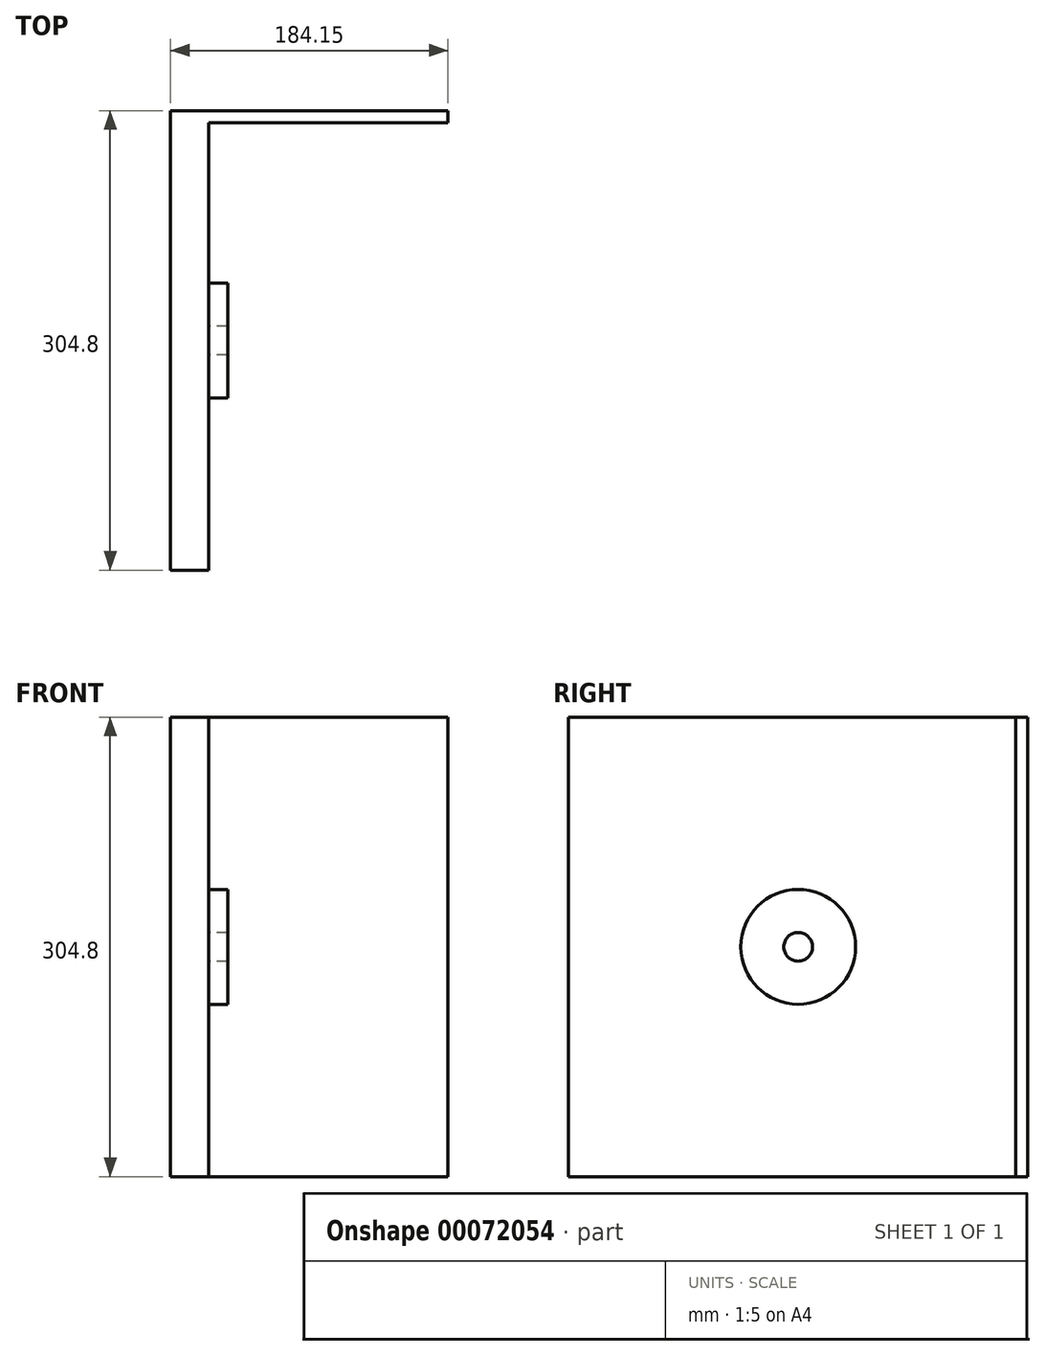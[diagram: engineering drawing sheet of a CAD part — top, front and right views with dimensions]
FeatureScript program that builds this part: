
annotation { "Feature Type Name" : "Feature", "Feature Type Description" : "" }
export const myFeature = defineFeature(function(context is Context, id is Id, definition is map)
    precondition{}
    {
        {
            var Q0;
            Q0=qCreatedBy(makeId("Right.planeOp"),FACE);
            var sketch = newSketch(context, id + "F0", { "sketchPlane" : qUnion([Q0])});
            skLineSegment(sketch, "E0.bottom", {"start": v(152.4, 152.4) * mm, "end": v(-152.4, 152.4) * mm});
            skLineSegment(sketch, "E0.top", {"start": v(152.4, -152.4) * mm, "end": v(-152.4, -152.4) * mm});
            skLineSegment(sketch, "E0.left", {"start": v(152.4, 152.4) * mm, "end": v(152.4, -152.4) * mm});
            skLineSegment(sketch, "E0.right", {"start": v(-152.4, 152.4) * mm, "end": v(-152.4, -152.4) * mm});
            skPoint(sketch, "E0.middle", {"position": v(0, 0) * mm});
            skSolve(sketch);
        }
        {
            var Q0;
            Q0=qSketchRegion(id+"F0",true);
            extrude(context, id + "F1", {"entities" : qUnion([Q0]), "depth" : 25.4 * mm});
        }
        {
            var Q0;
            Q0=makeQuery(id+"F1.opExtrude","CAP_FACE",FACE,{"disambiguationData":[OSD([sQuery(id+"F0.wireOp",EDGE,"E0.bottom"),sQuery(id+"F0.wireOp",EDGE,"E0.top"),sQuery(id+"F0.wireOp",EDGE,"E0.left"),sQuery(id+"F0.wireOp",EDGE,"E0.right")])],"isStart":false});
            var sketch = newSketch(context, id + "F2", { "sketchPlane" : qUnion([Q0])});
            skLineSegment(sketch, "E1.bottom", {"start": v(152.4, 152.4) * mm, "end": v(144.46, 152.4) * mm});
            skLineSegment(sketch, "E1.top", {"start": v(152.4, -152.4) * mm, "end": v(144.46, -152.4) * mm});
            skLineSegment(sketch, "E1.left", {"start": v(152.4, 152.4) * mm, "end": v(152.4, -152.4) * mm});
            skLineSegment(sketch, "E1.right", {"start": v(144.46, 152.4) * mm, "end": v(144.46, -152.4) * mm});
            skSolve(sketch);
        }
        {
            var Q0;
            Q0 = qSketchRegion(id + "F2", true);
            extrude(context, id + "F3", {"entities" : qUnion([Q0]), "operationType" : NewBodyOperationType.ADD, "depth" : 158.75 * mm});
        }
        {
            var Q0;
            Q0=makeQuery(id+"F1.opExtrude","CAP_FACE",FACE,{"disambiguationData":[OSD([sQuery(id+"F0.wireOp",EDGE,"E0.bottom"),sQuery(id+"F0.wireOp",EDGE,"E0.top"),sQuery(id+"F0.wireOp",EDGE,"E0.left"),sQuery(id+"F0.wireOp",EDGE,"E0.right")])],"isStart":false});
            var sketch = newSketch(context, id + "F4", { "sketchPlane" : qUnion([Q0])});
            skCircle(sketch, "E2", {"center": v(0, 0) * mm, "radius": 38.1 * mm});
            skSolve(sketch);
        }
        {
            var Q0;
            Q0 = qSketchRegion(id + "F4", true);
            extrude(context, id + "F5", {"entities" : qUnion([Q0]), "operationType" : NewBodyOperationType.ADD, "depth" : 12.7 * mm});
        }
        {
            var Q0;
            Q0=makeQuery(id+"F1.opExtrude","CAP_FACE",FACE,{"disambiguationData":[OSD([sQuery(id+"F0.wireOp",EDGE,"E0.bottom"),sQuery(id+"F0.wireOp",EDGE,"E0.top"),sQuery(id+"F0.wireOp",EDGE,"E0.left"),sQuery(id+"F0.wireOp",EDGE,"E0.right")])],"isStart":false});
            var sketch = newSketch(context, id + "F6", { "sketchPlane" : qUnion([Q0])});
            skCircle(sketch, "E3", {"center": v(0, 0) * mm, "radius": 9.53 * mm});
            skSolve(sketch);
        }
        {
            var Q0;
            Q0 = qSketchRegion(id + "F6", true);
            extrude(context, id + "F7", {"entities" : qUnion([Q0]), "operationType" : NewBodyOperationType.REMOVE, "depth" : 12.7 * mm});
        }
    });
